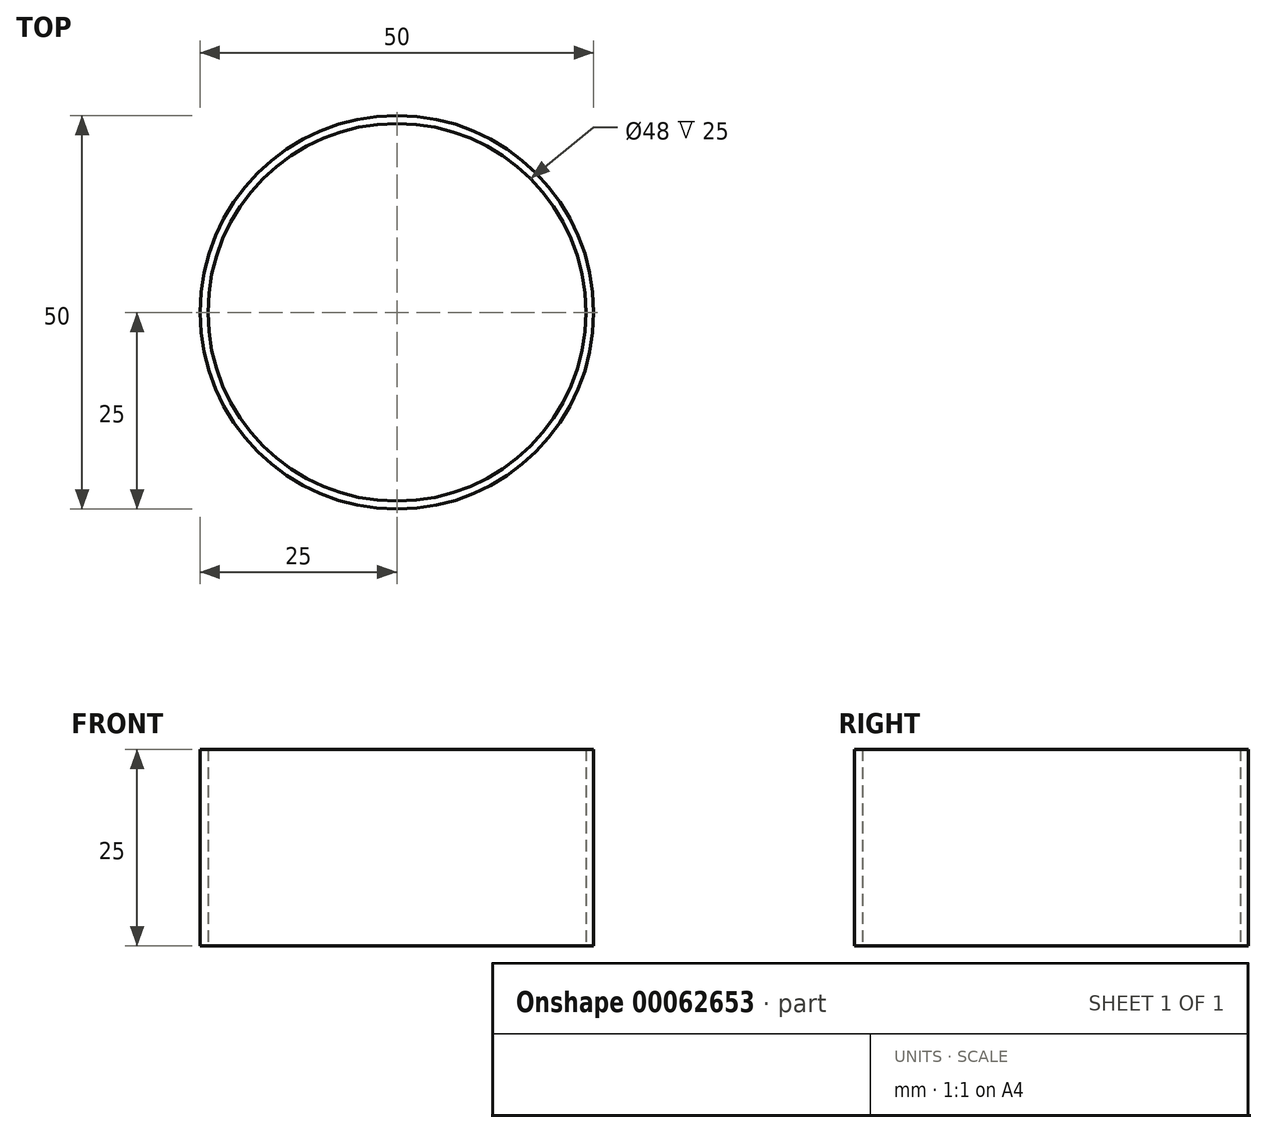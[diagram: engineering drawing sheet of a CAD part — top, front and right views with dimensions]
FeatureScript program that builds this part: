
annotation { "Feature Type Name" : "Feature", "Feature Type Description" : "" }
export const myFeature = defineFeature(function(context is Context, id is Id, definition is map)
    precondition{}
    {
        {
            var Q0;
            Q0=qCreatedBy(makeId("Top.planeOp"),FACE);
            var sketch = newSketch(context, id + "F0", { "sketchPlane" : qUnion([Q0])});
            skCircle(sketch, "E0", {"center": v(0, 0) * mm, "radius": 25 * mm});
            skCircle(sketch, "E1", {"center": v(0, 0) * mm, "radius": 24 * mm});
            skSolve(sketch);
        }
        {
            var Q0;
            Q0 = qSketchRegion(id + "F0", true);
            extrude(context, id + "F1", {"entities" : qUnion([Q0]), "depth" : 25 * mm});
        }
    });
